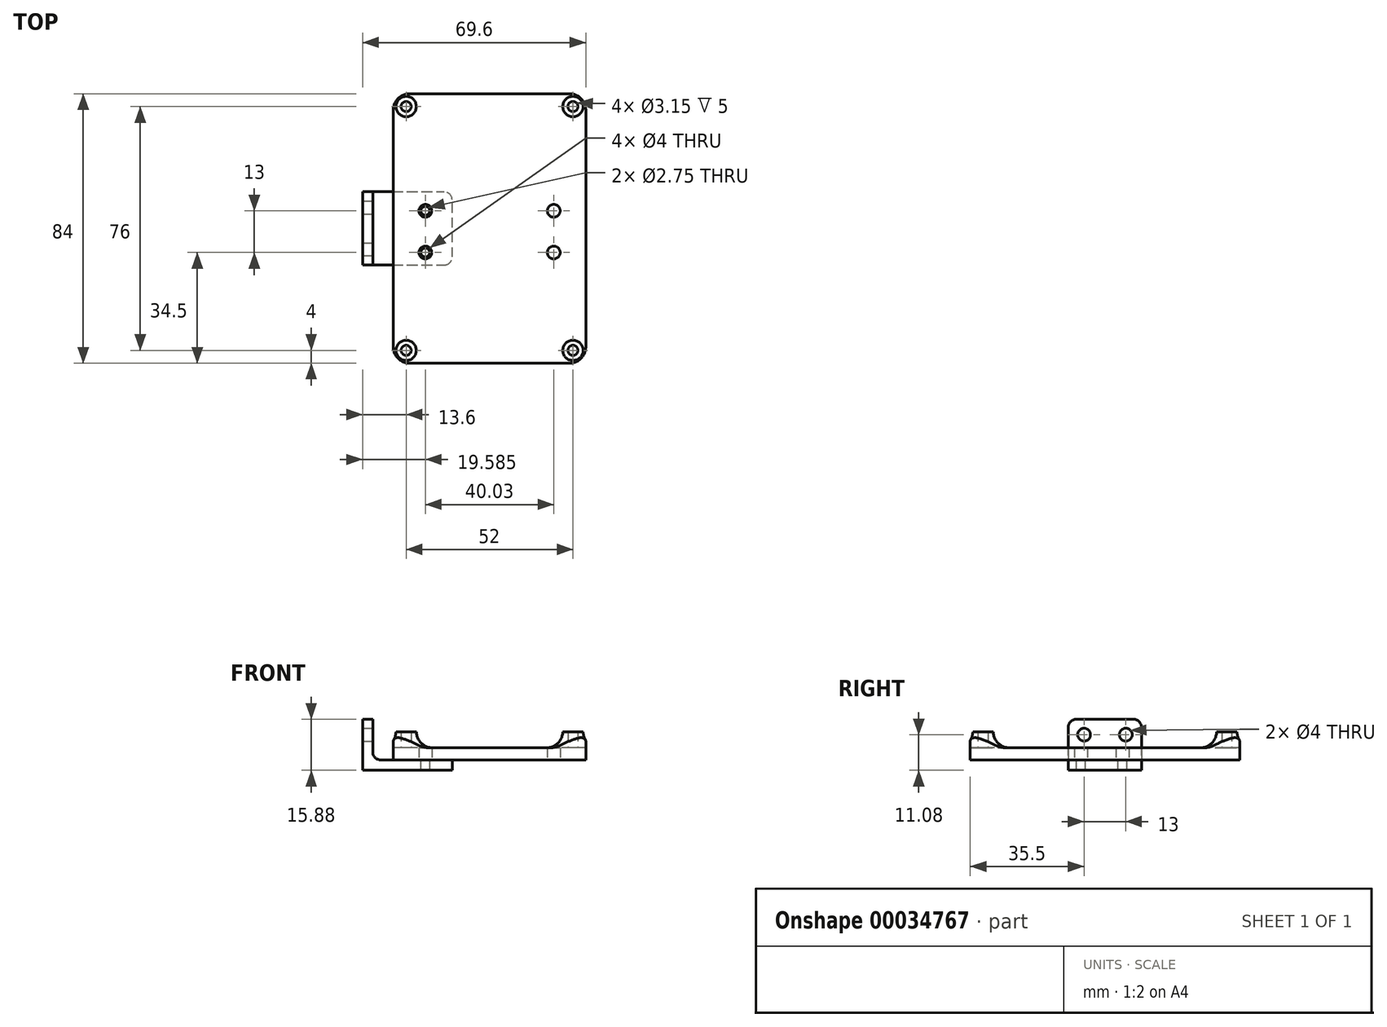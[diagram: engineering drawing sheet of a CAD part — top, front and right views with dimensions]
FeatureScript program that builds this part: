
annotation { "Feature Type Name" : "Feature", "Feature Type Description" : "" }
export const myFeature = defineFeature(function(context is Context, id is Id, definition is map)
    precondition{}
    {
        {
            var Q0;
            Q0=qCreatedBy(makeId("Top.planeOp"),FACE);
            var sketch = newSketch(context, id + "F0", { "sketchPlane" : qUnion([Q0]) });
            skLineSegment(sketch, "E0.bottom", {"start": v(-30, 42) * mm, "end": v(30, 42) * mm});
            skLineSegment(sketch, "E0.top", {"start": v(-30, -42) * mm, "end": v(30, -42) * mm});
            skLineSegment(sketch, "E0.left", {"start": v(-30, 42) * mm, "end": v(-30, -42) * mm});
            skLineSegment(sketch, "E0.right", {"start": v(30, 42) * mm, "end": v(30, -42) * mm});
            skLineSegment(sketch, "E1", {"start": v(-30, 42) * mm, "end": v(30, -42) * mm, "construction": true});
            skSolve(sketch);
        }
        {
            var Q0;
            Q0 = qSketchRegion(id + "F0", true);
            extrude(context, id + "F1", {"entities" : qUnion([Q0]), "depth" : 3.8 * mm});
        }
        {
            var Q0;
            Q0=makeQuery(id+"F1.opExtrude","CAP_FACE",FACE,{"disambiguationData":[OSD([sQuery(id+"F0.wireOp",EDGE,"E0.bottom"),sQuery(id+"F0.wireOp",EDGE,"E0.top"),sQuery(id+"F0.wireOp",EDGE,"E0.left"),sQuery(id+"F0.wireOp",EDGE,"E0.right")])],"isStart":false});
            var sketch = newSketch(context, id + "F2", { "sketchPlane" : qUnion([Q0]) });
            skLineSegment(sketch, "E2.bottom", {"start": v(-26, 38) * mm, "end": v(26, 38) * mm, "construction": true});
            skLineSegment(sketch, "E2.top", {"start": v(-26, -38) * mm, "end": v(26, -38) * mm, "construction": true});
            skLineSegment(sketch, "E2.left", {"start": v(-26, 38) * mm, "end": v(-26, -38) * mm, "construction": true});
            skLineSegment(sketch, "E2.right", {"start": v(26, 38) * mm, "end": v(26, -38) * mm, "construction": true});
            skLineSegment(sketch, "E3", {"start": v(-26, 38) * mm, "end": v(26, -38) * mm, "construction": true});
            skCircle(sketch, "E4", {"center": v(-26, 38) * mm, "radius": 3.18 * mm});
            skCircle(sketch, "E5", {"center": v(26, 38) * mm, "radius": 3.18 * mm});
            skCircle(sketch, "E6", {"center": v(26, -38) * mm, "radius": 3.18 * mm});
            skCircle(sketch, "E7", {"center": v(-26, -38) * mm, "radius": 3.18 * mm});
            skCircle(sketch, "E8", {"center": v(-26, 38) * mm, "radius": 1.57 * mm});
            skCircle(sketch, "E9", {"center": v(26, 38) * mm, "radius": 1.57 * mm});
            skCircle(sketch, "E10", {"center": v(26, -38) * mm, "radius": 1.57 * mm});
            skCircle(sketch, "E11", {"center": v(-26, -38) * mm, "radius": 1.57 * mm});
            skSolve(sketch);
        }
        {
            var Q0;
            Q0 = qSketchRegion(id + "F2", true);
            extrude(context, id + "F3", {"entities" : qUnion([Q0]), "operationType" : NewBodyOperationType.ADD, "depth" : 5 * mm});
        }
        {
            var Q0;
            Q0=makeQuery(id+"F1.opExtrude","CAP_FACE",FACE,{"disambiguationData":[OSD([sQuery(id+"F0.wireOp",EDGE,"E0.bottom"),sQuery(id+"F0.wireOp",EDGE,"E0.top"),sQuery(id+"F0.wireOp",EDGE,"E0.left"),sQuery(id+"F0.wireOp",EDGE,"E0.right")])],"isStart":true});
            var sketch = newSketch(context, id + "F4", { "sketchPlane" : qUnion([Q0]) });
            skLineSegment(sketch, "E12.bottom", {"start": v(-20.02, 7.5) * mm, "end": v(20.02, 7.5) * mm, "construction": true});
            skLineSegment(sketch, "E12.top", {"start": v(-20.02, -5.5) * mm, "end": v(20.02, -5.5) * mm, "construction": true});
            skLineSegment(sketch, "E12.left", {"start": v(-20.02, 7.5) * mm, "end": v(-20.02, -5.5) * mm, "construction": true});
            skLineSegment(sketch, "E12.right", {"start": v(20.02, 7.5) * mm, "end": v(20.02, -5.5) * mm, "construction": true});
            skCircle(sketch, "E13", {"center": v(-20.02, 7.5) * mm, "radius": 2 * mm});
            skCircle(sketch, "E14", {"center": v(20.02, 7.5) * mm, "radius": 2 * mm});
            skCircle(sketch, "E15", {"center": v(20.02, -5.5) * mm, "radius": 2 * mm});
            skCircle(sketch, "E16", {"center": v(-20.02, -5.5) * mm, "radius": 2 * mm});
            skLineSegment(sketch, "E17", {"start": v(0, 7.5) * mm, "end": v(0, 0) * mm, "construction": true});
            skSolve(sketch);
        }
        {
            var Q0;
            Q0 = qSketchRegion(id + "F4", true);
            var Q1;
            {var subQ0=sQuery(id+"F0.wireOp",EDGE,"E0.right");var subQ1=sQuery(id+"F0.wireOp",EDGE,"E0.left");var subQ2=sQuery(id+"F0.wireOp",EDGE,"E0.top");var subQ3=sQuery(id+"F0.wireOp",EDGE,"E0.bottom");Q1=makeQuery(id+"F3.boolean.opBoolean","SPLIT",FACE,{"disambiguationData":[TD([makeQuery(id+"F1.opExtrude","SWEPT_FACE",FACE,{"disambiguationData":[OSD([subQ3])]})])],"derivedFrom":makeQuery(id+"F1.opExtrude","CAP_FACE",FACE,{"disambiguationData":[OSD([subQ3,subQ2,subQ1,subQ0])],"isStart":false})});}
            extrude(context, id + "F5", {"entities" : qUnion([Q0]), "operationType" : NewBodyOperationType.REMOVE, "endBound" : BoundingType.UP_TO_SURFACE, "oppositeDirection" : true, "endBoundEntityFace" : qUnion([Q1]), "depth" : 25.4 * mm});
        }
        {
            var Q0;
            Q0=makeQuery(id+"F3.opExtrude","CAP_EDGE",EDGE,{"disambiguationData":[OSD([sQuery(id+"F2.wireOp",EDGE,"E6")])],"isStart":true});
            var Q1;
            Q1=makeQuery(id+"F3.opExtrude","CAP_EDGE",EDGE,{"disambiguationData":[OSD([sQuery(id+"F2.wireOp",EDGE,"E7")])],"isStart":true});
            var Q2;
            Q2=makeQuery(id+"F3.opExtrude","CAP_EDGE",EDGE,{"disambiguationData":[OSD([sQuery(id+"F2.wireOp",EDGE,"E4")])],"isStart":true});
            var Q3;
            Q3=makeQuery(id+"F3.opExtrude","CAP_EDGE",EDGE,{"disambiguationData":[OSD([sQuery(id+"F2.wireOp",EDGE,"E5")])],"isStart":true});
            fillet(context, id + "F6", {"entities" : qUnion([Q0, Q1, Q2, Q3]), "radius" : 5.08 * mm, "tangentPropagation" : true, "conicFillet" : false});
        }
        {
            var Q0;
            Q0=makeQuery(id+"F1.opExtrude","SWEPT_EDGE",EDGE,{"disambiguationData":[OSD([sQuery(id+"F0.wireOp",EDGE,"E0.top"),sQuery(id+"F0.wireOp",EDGE,"E0.left")])]});
            var Q1;
            Q1=makeQuery(id+"F1.opExtrude","SWEPT_EDGE",EDGE,{"disambiguationData":[OSD([sQuery(id+"F0.wireOp",EDGE,"E0.top"),sQuery(id+"F0.wireOp",EDGE,"E0.right")])]});
            var Q2;
            Q2=makeQuery(id+"F1.opExtrude","SWEPT_EDGE",EDGE,{"disambiguationData":[OSD([sQuery(id+"F0.wireOp",EDGE,"E0.bottom"),sQuery(id+"F0.wireOp",EDGE,"E0.right")])]});
            var Q3;
            Q3=makeQuery(id+"F1.opExtrude","SWEPT_EDGE",EDGE,{"disambiguationData":[OSD([sQuery(id+"F0.wireOp",EDGE,"E0.bottom"),sQuery(id+"F0.wireOp",EDGE,"E0.left")])]});
            fillet(context, id + "F7", {"entities" : qUnion([Q0, Q1, Q2, Q3]), "radius" : 5.08 * mm, "tangentPropagation" : true, "conicFillet" : false});
        }
        {
            var Q0;
            Q0=makeQuery(id+"F1.opExtrude","CAP_FACE",FACE,{"disambiguationData":[OSD([sQuery(id+"F0.wireOp",EDGE,"E0.bottom"),sQuery(id+"F0.wireOp",EDGE,"E0.top"),sQuery(id+"F0.wireOp",EDGE,"E0.left"),sQuery(id+"F0.wireOp",EDGE,"E0.right")])],"isStart":true});
            var sketch = newSketch(context, id + "F8", { "sketchPlane" : qUnion([Q0]) });
            skLineSegment(sketch, "E18.bottom", {"start": v(-39.6, 11.43) * mm, "end": v(-11.66, 11.43) * mm});
            skLineSegment(sketch, "E18.top", {"start": v(-39.6, -11.43) * mm, "end": v(-11.66, -11.43) * mm});
            skLineSegment(sketch, "E18.left", {"start": v(-39.6, 11.43) * mm, "end": v(-39.6, -11.43) * mm});
            skLineSegment(sketch, "E18.right", {"start": v(-11.66, 11.43) * mm, "end": v(-11.66, -11.43) * mm});
            skLineSegment(sketch, "E19", {"start": v(-11.66, 0) * mm, "end": v(0, 0) * mm});
            skSolve(sketch);
        }
        {
            var Q0;
            Q0 = qSketchRegion(id + "F8", true);
            extrude(context, id + "F9", {"entities" : qUnion([Q0]), "depth" : 3.17 * mm});
        }
        {
            var Q0;
            Q0=makeQuery(id+"F9.opExtrude","CAP_FACE",FACE,{"disambiguationData":[OSD([sQuery(id+"F8.wireOp",EDGE,"E18.bottom"),sQuery(id+"F8.wireOp",EDGE,"E18.top"),sQuery(id+"F8.wireOp",EDGE,"E18.left"),sQuery(id+"F8.wireOp",EDGE,"E18.right")])],"isStart":true});
            var sketch = newSketch(context, id + "F10", { "sketchPlane" : qUnion([Q0]) });
            skLineSegment(sketch, "E20.bottom", {"start": v(-39.6, 11.43) * mm, "end": v(-36.43, 11.43) * mm});
            skLineSegment(sketch, "E20.top", {"start": v(-39.6, -11.43) * mm, "end": v(-36.43, -11.43) * mm});
            skLineSegment(sketch, "E20.left", {"start": v(-39.6, 11.43) * mm, "end": v(-39.6, -11.43) * mm});
            skLineSegment(sketch, "E20.right", {"start": v(-36.43, 11.43) * mm, "end": v(-36.43, -11.43) * mm});
            skSolve(sketch);
        }
        {
            var Q0;
            Q0 = qSketchRegion(id + "F10", true);
            extrude(context, id + "F11", {"entities" : qUnion([Q0]), "operationType" : NewBodyOperationType.ADD, "depth" : 12.7 * mm});
        }
        {
            var Q0;
            Q0=makeQuery(id+"F9.opExtrude","CAP_FACE",FACE,{"disambiguationData":[OSD([sQuery(id+"F8.wireOp",EDGE,"E18.bottom"),sQuery(id+"F8.wireOp",EDGE,"E18.top"),sQuery(id+"F8.wireOp",EDGE,"E18.left"),sQuery(id+"F8.wireOp",EDGE,"E18.right")])],"isStart":true});
            var sketch = newSketch(context, id + "F12", { "sketchPlane" : qUnion([Q0]) });
            skCircle(sketch, "E21.0", {"center": v(-20.02, 5.5) * mm, "radius": 2 * mm, "construction": true});
            skCircle(sketch, "E22.0", {"center": v(-20.02, -7.5) * mm, "radius": 2 * mm, "construction": true});
            skCircle(sketch, "E23", {"center": v(-20.02, 5.5) * mm, "radius": 1.38 * mm});
            skCircle(sketch, "E24", {"center": v(-20.02, -7.5) * mm, "radius": 1.38 * mm});
            skSolve(sketch);
        }
        {
            var Q0;
            Q0=makeQuery(id+"F11.opExtrude","SWEPT_FACE",FACE,{"disambiguationData":[OSD([sQuery(id+"F10.wireOp",EDGE,"E20.right")])]});
            var sketch = newSketch(context, id + "F13", { "sketchPlane" : qUnion([Q0]) });
            skCircle(sketch, "E25", {"center": v(-6.5, 7.9) * mm, "radius": 2 * mm});
            skCircle(sketch, "E26", {"center": v(6.5, 7.9) * mm, "radius": 2 * mm});
            skLineSegment(sketch, "E27", {"start": v(-6.5, 7.9) * mm, "end": v(6.5, 7.9) * mm, "construction": true});
            skLineSegment(sketch, "E28", {"start": v(0, 0) * mm, "end": v(0, 7.9) * mm, "construction": true});
            skSolve(sketch);
        }
        {
            var Q0;
            Q0 = qSketchRegion(id + "F12", true);
            extrude(context, id + "F14", {"entities" : qUnion([Q0]), "operationType" : NewBodyOperationType.REMOVE, "endBound" : BoundingType.UP_TO_NEXT, "oppositeDirection" : true, "depth" : 25.4 * mm});
        }
        {
            var Q0;
            Q0 = qSketchRegion(id + "F13", true);
            extrude(context, id + "F15", {"entities" : qUnion([Q0]), "operationType" : NewBodyOperationType.REMOVE, "endBound" : BoundingType.UP_TO_NEXT, "oppositeDirection" : true, "depth" : 25.4 * mm});
        }
        {
            var Q0;
            Q0=makeQuery(id+"F11.opExtrude","CAP_EDGE",EDGE,{"disambiguationData":[OSD([sQuery(id+"F10.wireOp",EDGE,"E20.right")])],"isStart":true});
            fillet(context, id + "F16", {"entities" : qUnion([Q0]), "radius" : 2.54 * mm, "tangentPropagation" : true, "conicFillet" : false});
        }
        {
            var Q0;
            Q0=makeQuery(id+"F9.opExtrude","SWEPT_EDGE",EDGE,{"disambiguationData":[OSD([sQuery(id+"F8.wireOp",EDGE,"E18.bottom"),sQuery(id+"F8.wireOp",EDGE,"E18.right")])]});
            var Q1;
            Q1=makeQuery(id+"F9.opExtrude","SWEPT_EDGE",EDGE,{"disambiguationData":[OSD([sQuery(id+"F8.wireOp",EDGE,"E18.top"),sQuery(id+"F8.wireOp",EDGE,"E18.right")])]});
            var Q2;
            Q2=makeQuery(id+"F11.opExtrude","CAP_EDGE",EDGE,{"disambiguationData":[OSD([sQuery(id+"F10.wireOp",EDGE,"E20.bottom")])],"isStart":false});
            var Q3;
            Q3=makeQuery(id+"F11.opExtrude","CAP_EDGE",EDGE,{"disambiguationData":[OSD([sQuery(id+"F10.wireOp",EDGE,"E20.top")])],"isStart":false});
            fillet(context, id + "F17", {"entities" : qUnion([Q0, Q1, Q2, Q3]), "radius" : 2.54 * mm, "tangentPropagation" : true, "conicFillet" : false});
        }
    });
